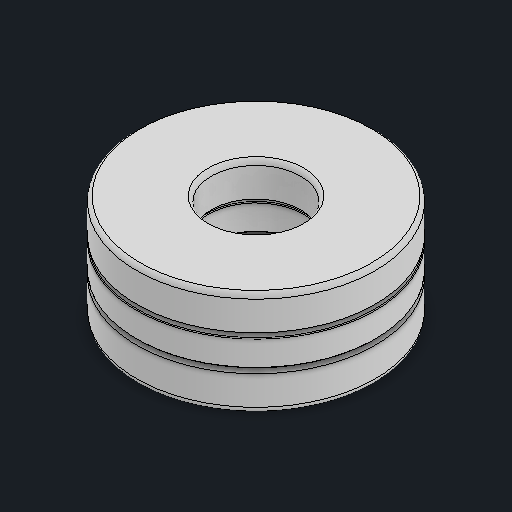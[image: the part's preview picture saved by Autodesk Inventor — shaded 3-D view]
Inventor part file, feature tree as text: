
AUTODESK INVENTOR PART (.ipt)
format: ipt  version: 2024 (Build 280153000, 153)  size: 457,216 bytes
history: native  units: in
note: dims shown in document units (in); Inventor stores cm internally (conversion verified against a paired STEP export)
features: other x5, revolve x3, pattern_circular x1
ambient origin geometry x8: Origin, YZ Plane, XZ Plane, XY Plane, X Axis, Y Axis, Z Axis, Center Point
bodies: Solid1 (feature_tree), Solid2 (feature_tree), Solid3 (feature_tree), Solid4 (feature_tree), Solid5 (feature_tree), Solid6 (feature_tree), Solid7 (feature_tree), Solid8 (feature_tree), Solid9 (feature_tree)
feature tree (9):
  revolve  "Revolve1[1]"  [1 undecoded]
  revolve  "Revolve1[2]"  [1 undecoded]
  revolve  "Revolve2"  [1 undecoded]
  other  "CirPattern1[1]"
  other  "CirPattern1[2]"
  other  "CirPattern1[3]"
  other  "CirPattern1[4]"
  other  "CirPattern1[5]"
  pattern_circular  "CirPattern2"
note: 3 required parameter values undecoded (feature->parameter linkage not recoverable at this tier; creation-order binding heuristic only, values carry confidence <= 0.55)
